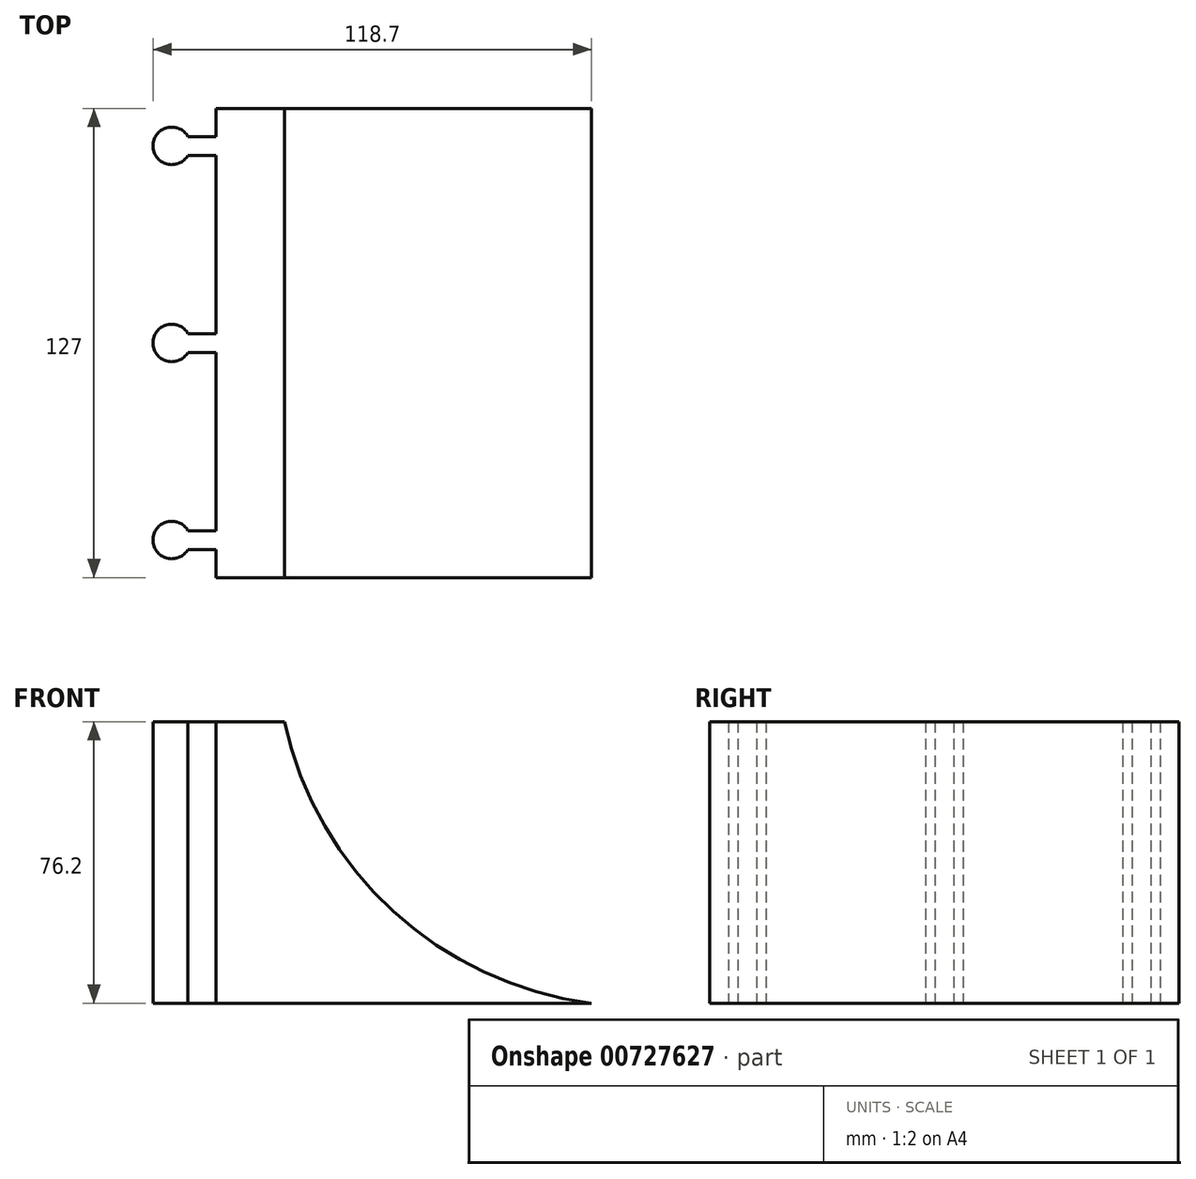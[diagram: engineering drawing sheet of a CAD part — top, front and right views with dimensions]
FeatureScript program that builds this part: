
annotation { "Feature Type Name" : "Feature", "Feature Type Description" : "" }
export const myFeature = defineFeature(function(context is Context, id is Id, definition is map)
    precondition{}
    {
        {
            var Q0;
            Q0=qCreatedBy(makeId("Top.planeOp"),FACE);
            var sketch = newSketch(context, id + "F0", { "sketchPlane" : qUnion([Q0])});
            skLineSegment(sketch, "E0.bottom", {"start": v(-69.35, 52.05) * mm, "end": v(32.25, 52.05) * mm});
            skLineSegment(sketch, "E0.top", {"start": v(-69.35, -49.55) * mm, "end": v(32.25, -49.55) * mm});
            skLineSegment(sketch, "E0.left", {"start": v(-69.35, 52.05) * mm, "end": v(-69.35, -49.55) * mm});
            skLineSegment(sketch, "E0.right", {"start": v(32.25, 52.05) * mm, "end": v(32.25, -49.55) * mm});
            skSolve(sketch);
        }
        {
            var Q0;
            Q0 = qSketchRegion(id + "F0", true);
            extrude(context, id + "F1", {"entities" : qUnion([Q0]), "depth" : 76.2 * mm, "offsetDistance" : 25.4 * mm});
        }
        {
            var Q0;
            Q0=makeQuery(id+"F1.opExtrude","SWEPT_FACE",FACE,{"disambiguationData":[OSD([sQuery(id+"F0.wireOp",EDGE,"E0.top")])]});
            var sketch = newSketch(context, id + "F2", { "sketchPlane" : qUnion([Q0])});
            skArc(sketch, "E1", {"start": v(-50.9, 76.2) * mm, "mid": v(-21.44, 24.88) * mm, "end": v(32.25, 0) * mm});
            skSolve(sketch);
        }
        {
            var Q0;
            {var subQ0=sQuery(id+"F2.wireOp",EDGE,"JlhNct4V-yrV0-lDqy-Yc6o-JnxJMGN9b7yu");Q0=makeQuery(id+"F2.imprint","IMPRINT",FACE,{"disambiguationData":[TD([[makeQuery(id+"F2.imprint","IMPRINT",EDGE,{"derivedFrom":subQ0}),1.0]])]});}
            var Q1;
            {var subQ0=sQuery(id+"F2.wireOp",EDGE,"E1");Q1=makeQuery(id+"F2.imprint","IMPRINT",FACE,{"disambiguationData":[TD([[makeQuery(id+"F2.imprint","IMPRINT",EDGE,{"derivedFrom":subQ0}),1.0]])]});}
            extrude(context, id + "F3", {"entities" : qUnion([Q0, Q1]), "operationType" : NewBodyOperationType.REMOVE, "oppositeDirection" : true, "depth" : 101.6 * mm, "offsetDistance" : 25.4 * mm});
        }
        {
            var Q0;
            Q0=makeQuery(id+"F1.opExtrude","CAP_FACE",FACE,{"disambiguationData":[OSD([sQuery(id+"F0.wireOp",EDGE,"E0.bottom"),sQuery(id+"F0.wireOp",EDGE,"E0.top"),sQuery(id+"F0.wireOp",EDGE,"E0.left"),sQuery(id+"F0.wireOp",EDGE,"E0.right")])],"isStart":true});
            var sketch = newSketch(context, id + "F4", { "sketchPlane" : qUnion([Q0])});
            skLineSegment(sketch, "E2.bottom", {"start": v(-63.56, 42.29) * mm, "end": v(0, 42.29) * mm});
            skLineSegment(sketch, "E2.top", {"start": v(-63.56, -46.58) * mm, "end": v(0, -46.58) * mm});
            skLineSegment(sketch, "E2.left", {"start": v(-63.56, 42.29) * mm, "end": v(-63.56, -46.58) * mm});
            skLineSegment(sketch, "E2.right", {"start": v(0, 42.29) * mm, "end": v(0, -46.58) * mm});
            skSolve(sketch);
        }
        {
            var Q0;
            Q0=makeQuery(id+"F4.imprint","IMPRINT",FACE,{"disambiguationData":[TD([[makeQuery(id+"F4.imprint","IMPRINT",EDGE,{"derivedFrom":sQuery(id+"F4.wireOp",EDGE,"E2.bottom")}),-1.0]])]});
            extrude(context, id + "F5", {"entities" : qUnion([Q0]), "operationType" : NewBodyOperationType.ADD, "oppositeDirection" : true, "depth" : 7.62 * mm, "offsetDistance" : 25.4 * mm});
        }
        {
            var Q0;
            Q0=makeQuery(id+"F1.opExtrude","SWEPT_FACE",FACE,{"disambiguationData":[OSD([sQuery(id+"F0.wireOp",EDGE,"E0.top")])]});
            var sketch = newSketch(context, id + "F6", { "sketchPlane" : qUnion([Q0])});
            skSolve(sketch);
        }
        {
            var Q0;
            {var subQ0=sQuery(id+"F0.wireOp",EDGE,"E0.top");Q0=makeQuery(id+"F6.imprint","IMPRINT",FACE,{"disambiguationData":[TD([[makeQuery(id+"F6.imprint","IMPRINT",EDGE,{"derivedFrom":makeQuery(id+"F1.opExtrude","CAP_EDGE",EDGE,{"disambiguationData":[OSD([subQ0])],"isStart":true})}),1.0]])]});}
            extrude(context, id + "F7", {"entities" : qUnion([Q0]), "operationType" : NewBodyOperationType.ADD, "depth" : 25.4 * mm, "offsetDistance" : 25.4 * mm});
        }
        {
            var Q0;
            {var subQ0=sQuery(id+"F0.wireOp",EDGE,"E0.top");Q0=makeQuery(id+"F7.boolean.opBoolean","MERGE",FACE,{"derivedFrom":[makeQuery(id+"F1.opExtrude","CAP_FACE",FACE,{"disambiguationData":[OSD([sQuery(id+"F0.wireOp",EDGE,"E0.bottom"),subQ0,sQuery(id+"F0.wireOp",EDGE,"E0.left"),sQuery(id+"F0.wireOp",EDGE,"E0.right")])],"isStart":true}),makeQuery(id+"F7.opExtrude","SWEPT_FACE",FACE,{"disambiguationData":[OSD([subQ0]),TDD([makeQuery(id+"F6.imprint","IMPRINT",EDGE,{"derivedFrom":makeQuery(id+"F1.opExtrude","CAP_EDGE",EDGE,{"disambiguationData":[OSD([subQ0])],"isStart":true})})])]})]});}
            var sketch = newSketch(context, id + "F8", { "sketchPlane" : qUnion([Q0])});
            skLineSegment(sketch, "E3.bottom", {"start": v(-69.35, 14) * mm, "end": v(-76.97, 14) * mm});
            skLineSegment(sketch, "E3.top", {"start": v(-69.35, 8.91) * mm, "end": v(-76.97, 8.91) * mm});
            skLineSegment(sketch, "E3.left", {"start": v(-69.35, 8.91) * mm, "end": v(-69.35, 14) * mm});
            skLineSegment(sketch, "E3.right", {"start": v(-76.97, 8.91) * mm, "end": v(-76.97, 14) * mm});
            skLineSegment(sketch, "E4.bottom", {"start": v(-69.35, -44.43) * mm, "end": v(-76.97, -44.43) * mm});
            skLineSegment(sketch, "E4.top", {"start": v(-69.35, -39.35) * mm, "end": v(-76.97, -39.35) * mm});
            skLineSegment(sketch, "E4.left", {"start": v(-69.35, -44.43) * mm, "end": v(-69.35, -39.35) * mm});
            skLineSegment(sketch, "E4.right", {"start": v(-76.97, -44.43) * mm, "end": v(-76.97, -39.35) * mm});
            skLineSegment(sketch, "E5.bottom", {"start": v(-69.35, 62.25) * mm, "end": v(-76.97, 62.25) * mm});
            skLineSegment(sketch, "E5.top", {"start": v(-69.35, 67.33) * mm, "end": v(-76.97, 67.33) * mm});
            skLineSegment(sketch, "E5.left", {"start": v(-69.35, 62.25) * mm, "end": v(-69.35, 67.33) * mm});
            skLineSegment(sketch, "E5.right", {"start": v(-76.97, 62.25) * mm, "end": v(-76.97, 67.33) * mm});
            skArc(sketch, "E6", {"start": v(-76.97, 14) * mm, "mid": v(-86.45, 11.45) * mm, "end": v(-76.97, 8.91) * mm});
            skArc(sketch, "E7", {"start": v(-76.97, -39.35) * mm, "mid": v(-86.45, -41.89) * mm, "end": v(-76.97, -44.43) * mm});
            skArc(sketch, "E8", {"start": v(-76.97, 67.33) * mm, "mid": v(-86.45, 64.8) * mm, "end": v(-76.97, 62.25) * mm});
            skSolve(sketch);
        }
        {
            var Q0;
            Q0=makeQuery(id+"F8.imprint","IMPRINT",FACE,{"disambiguationData":[TD([[makeQuery(id+"F8.imprint","IMPRINT",EDGE,{"derivedFrom":sQuery(id+"F8.wireOp",EDGE,"E4.right")}),1.0]])]});
            var Q1;
            Q1=makeQuery(id+"F8.imprint","IMPRINT",FACE,{"disambiguationData":[TD([[makeQuery(id+"F8.imprint","IMPRINT",EDGE,{"derivedFrom":sQuery(id+"F8.wireOp",EDGE,"E4.bottom")}),-1.0]])]});
            var Q2;
            Q2=makeQuery(id+"F8.imprint","IMPRINT",FACE,{"disambiguationData":[TD([[makeQuery(id+"F8.imprint","IMPRINT",EDGE,{"derivedFrom":sQuery(id+"F8.wireOp",EDGE,"E3.right")}),1.0]])]});
            var Q3;
            Q3=makeQuery(id+"F8.imprint","IMPRINT",FACE,{"disambiguationData":[TD([[makeQuery(id+"F8.imprint","IMPRINT",EDGE,{"derivedFrom":sQuery(id+"F8.wireOp",EDGE,"E3.bottom")}),1.0]])]});
            var Q4;
            Q4=makeQuery(id+"F8.imprint","IMPRINT",FACE,{"disambiguationData":[TD([[makeQuery(id+"F8.imprint","IMPRINT",EDGE,{"derivedFrom":sQuery(id+"F8.wireOp",EDGE,"E5.bottom")}),-1.0]])]});
            var Q5;
            Q5=makeQuery(id+"F8.imprint","IMPRINT",FACE,{"disambiguationData":[TD([[makeQuery(id+"F8.imprint","IMPRINT",EDGE,{"derivedFrom":sQuery(id+"F8.wireOp",EDGE,"E5.right")}),1.0]])]});
            extrude(context, id + "F9", {"entities" : qUnion([Q0, Q1, Q2, Q3, Q4, Q5]), "operationType" : NewBodyOperationType.ADD, "oppositeDirection" : true, "depth" : 76.2 * mm, "offsetDistance" : 25.4 * mm});
        }
    });
